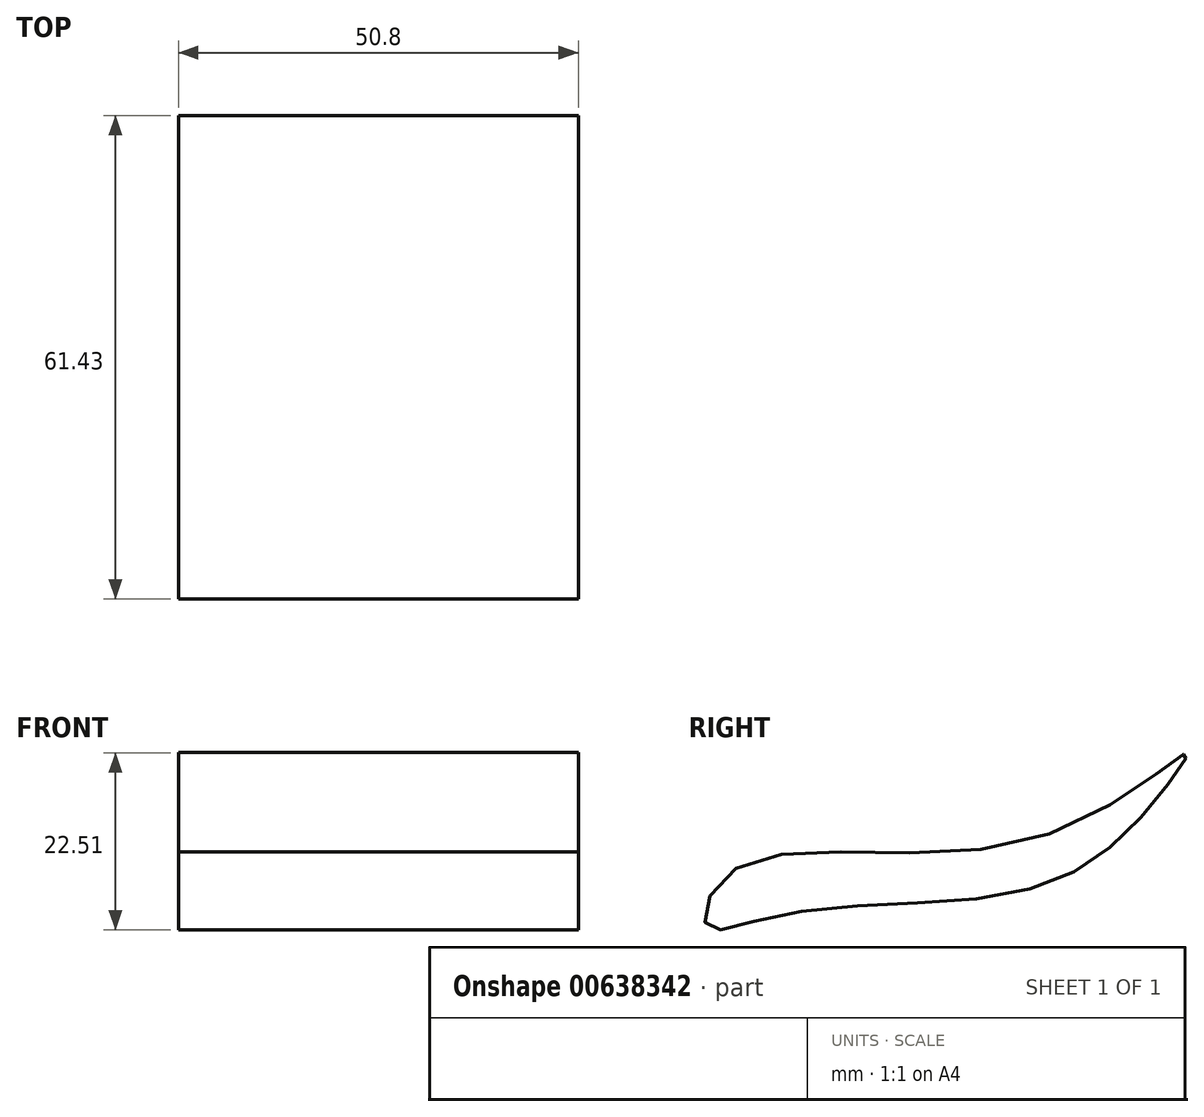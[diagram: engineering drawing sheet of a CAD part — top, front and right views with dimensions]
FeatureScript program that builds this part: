
annotation { "Feature Type Name" : "Feature", "Feature Type Description" : "" }
export const myFeature = defineFeature(function(context is Context, id is Id, definition is map)
    precondition{}
    {
        {
            var Q0;
            Q0=qCreatedBy(makeId("Right.planeOp"),FACE);
            var sketch = newSketch(context, id + "F0", { "sketchPlane" : qUnion([Q0])});
            skFitSpline(sketch, "E0", {"points": [v(-61.38, -14.66) * mm, v(-23.41, -10.9) * mm, v(-4.05, 0) * mm, v(-8.75, -6.77) * mm, v(-23.98, -17.3) * mm, v(-55.18, -20.5) * mm, v(-65.14, -22) * mm, v(-61.38, -14.66) * mm]});
            skSolve(sketch);
        }
        {
            var Q0;
            Q0=makeQuery(id+"F0.imprint","IMPRINT",FACE,{"disambiguationData":[TD([[makeQuery(id+"F0.imprint","IMPRINT",EDGE,{"derivedFrom":sQuery(id+"F0.wireOp",EDGE,"E0")}),-1.0]])]});
            extrude(context, id + "F1", {"entities" : qUnion([Q0]), "depth" : 50.8 * mm, "offsetDistance" : 25.4 * mm});
        }
    });
